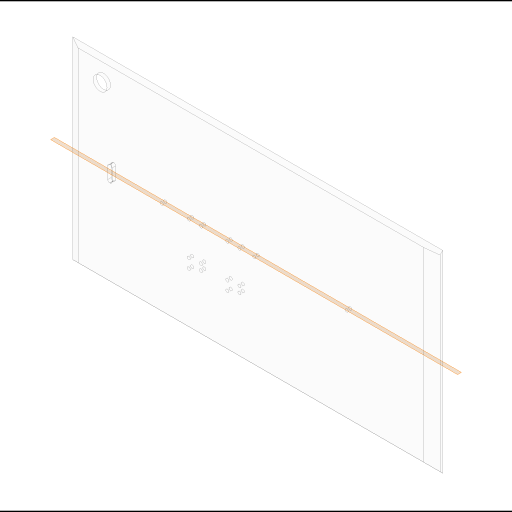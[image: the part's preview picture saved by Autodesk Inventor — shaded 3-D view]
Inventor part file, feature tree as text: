
AUTODESK INVENTOR PART (.ipt)
format: ipt  version: 2023 (Build 270158000, 158)  size: 216,576 bytes
history: native  units: in
note: dims shown in document units (in); Inventor stores cm internally (conversion verified against a paired STEP export)
features: extrude x7, sketch x7, projected_geometry x3, other x1
ambient origin geometry x8: Origin, YZ Plane, XZ Plane, XY Plane, X Axis, Y Axis, Z Axis, Center Point
bodies: Solid1 (feature_tree)
feature tree (18):
  extrude  "Extrusion1"  Depth=12.515in
  extrude  "Extrusion2"  Depth=0.227in
  extrude  "Extrusion3"  TaperAngle=0.0deg  [1 undecoded]
  other  "Center Plane"
  extrude  "Extrusion4"  TaperAngle=135.0deg  [1 undecoded]
  extrude  "Extrusion5"  Depth=6.2575in
  extrude  "Extrusion6"  Depth=0.0205in
  extrude  "Extrusion7"  Depth=0.3937in
  sketch  "Sketch1"  dims[d0=24.0in d1=12.515in]
  sketch  "Sketch2"  dims[d2=0.227in d3=0.0in d4=0.1494in]
  projected_geometry  "Projected Loop1"
  sketch  "Sketch3"  dims[d5=90.0deg d6=0.0in d7=0.0in]
  projected_geometry  "Projected Loop2"
  sketch  "Sketch4"  dims[d8=135.0deg d9=135.0deg]
  projected_geometry  "Projected Loop3"
  sketch  "Sketch5"  dims[d10=0.0in d11=0.0in d12=6.2575in]
  sketch  "Sketch6"  dims[d13=1.0in d14=0.0205in]
  sketch  "Sketch7"  dims[d15=6.083in d16=0.0in d17=7.75in d18=6.258in d19=0.197in d20=2.5in d21=0.197in d22=2.18in d23=2.18in d24=7.75in d25=2.5in d26=6.2575in d27=0.197in d28=0.197in d29=0.6in d30=0.6in d31=0.197in d32=0.197in d33=2.5in d34=7.75in d35=6.0in d36=0.197in d37=6.2575in d38=12.0in d39=0.197in d40=6.2575in d41=18.0in d42=6.2575in d43=0.197in d44=0.125in d45=0.2756in d46=0.7874in d47=6.258in d48=2.5in d49=0.0in d50=0.0in d51=1.5in d52=2.0in d53=0.9in d54=0.0in d55=0.0in d56=0.1969in d57=0.7874in d58=0.1969in d59=0.1969in d60=2.5in d61=0.1969in d62=0.1969in d63=0.1969in d64=2.5in d65=2.5in d66=0.3937in d67=180.0deg d68=0.3937in d69=0.0in d70=0.0in]
note: 2 required parameter values undecoded (feature->parameter linkage not recoverable at this tier; creation-order binding heuristic only, values carry confidence <= 0.55)
